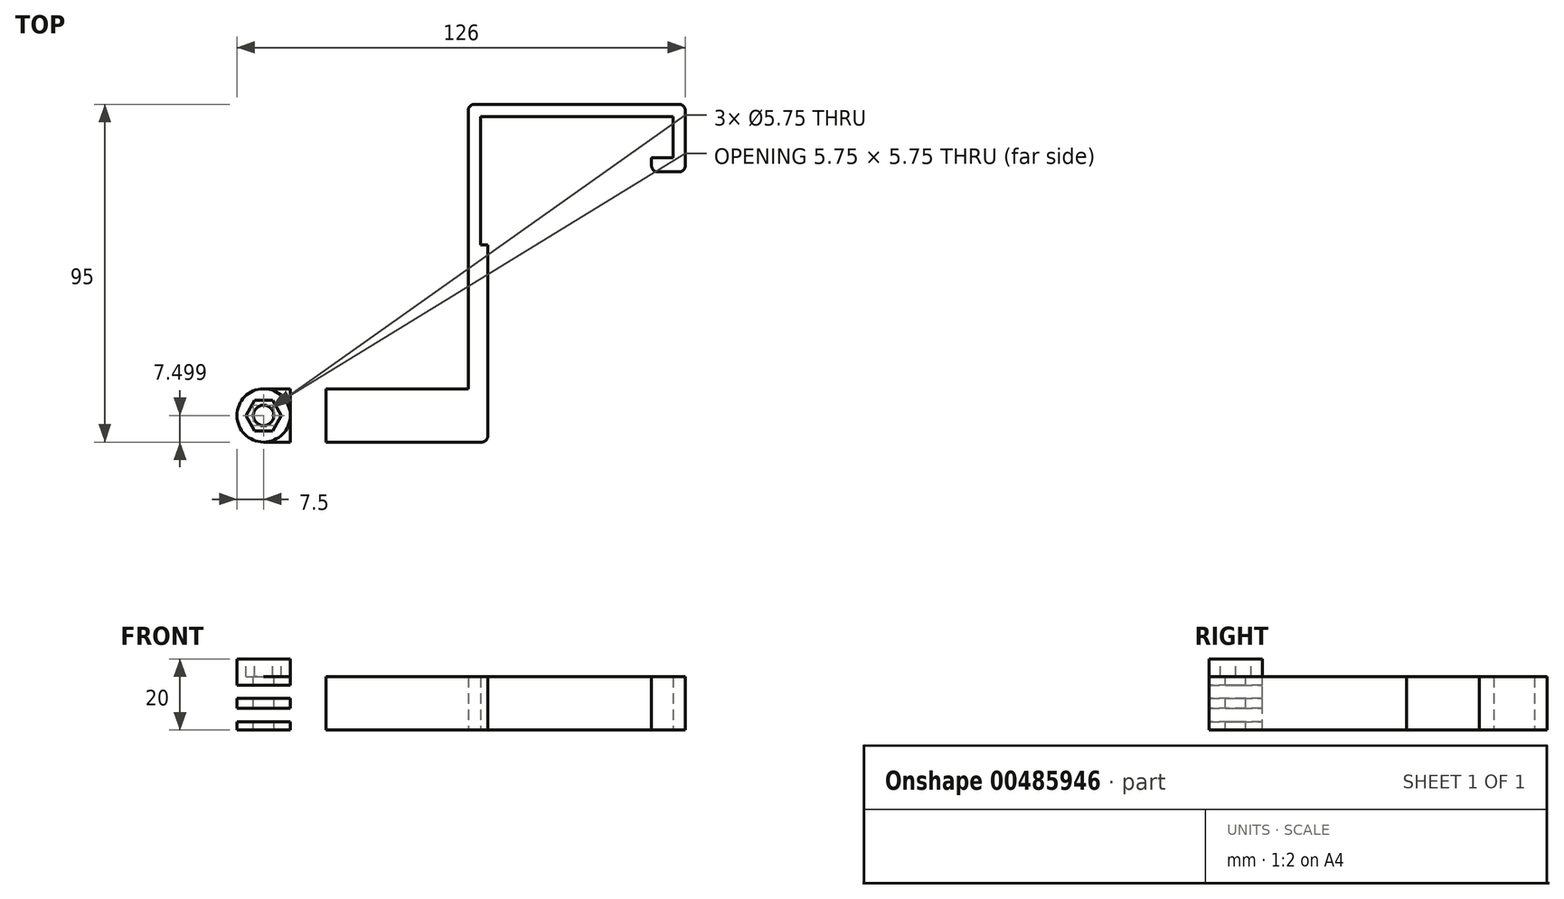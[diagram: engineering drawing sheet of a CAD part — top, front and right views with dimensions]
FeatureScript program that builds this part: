
annotation { "Feature Type Name" : "Feature", "Feature Type Description" : "" }
export const myFeature = defineFeature(function(context is Context, id is Id, definition is map)
    precondition{}
    {
        {
            var Q0;
            Q0=qCreatedBy(makeId("Top.planeOp"),FACE);
            var sketch = newSketch(context, id + "F0", { "sketchPlane" : qUnion([Q0])});
            skLineSegment(sketch, "E0", {"start": v(-30, 3.99) * mm, "end": v(31, 3.99) * mm});
            skLineSegment(sketch, "E1", {"start": v(-26.5, 0.49) * mm, "end": v(27.5, 0.49) * mm});
            skLineSegment(sketch, "E2", {"start": v(27.5, 0.49) * mm, "end": v(27.5, -11.01) * mm});
            skLineSegment(sketch, "E3", {"start": v(-26.5, 0.49) * mm, "end": v(-26.5, -66.01) * mm});
            skLineSegment(sketch, "E4", {"start": v(27.5, -11.01) * mm, "end": v(21.5, -11.01) * mm});
            skLineSegment(sketch, "E5", {"start": v(21.5, -11.01) * mm, "end": v(21.5, -15.01) * mm});
            skLineSegment(sketch, "E6", {"start": v(21.5, -15.01) * mm, "end": v(31, -15.01) * mm});
            skLineSegment(sketch, "E7", {"start": v(31, 3.99) * mm, "end": v(31, -15.01) * mm});
            skLineSegment(sketch, "E8", {"start": v(-26.5, -66.01) * mm, "end": v(-19.5, -66.01) * mm});
            skLineSegment(sketch, "E9", {"start": v(-19.5, -66.01) * mm, "end": v(-19.5, -91.01) * mm});
            skLineSegment(sketch, "E10", {"start": v(-19.5, -91.01) * mm, "end": v(-30, -91.01) * mm});
            skLineSegment(sketch, "E11", {"start": v(-30, 3.99) * mm, "end": v(-30, -91.01) * mm});
            skLineSegment(sketch, "E12", {"start": v(-26.5, -66.01) * mm, "end": v(-26.5, -76.01) * mm});
            skLineSegment(sketch, "E13", {"start": v(-26.5, -76.01) * mm, "end": v(-19.5, -76.01) * mm});
            skLineSegment(sketch, "E14", {"start": v(-26.5, -76.01) * mm, "end": v(-26.5, -91.01) * mm});
            skLineSegment(sketch, "E15", {"start": v(-23, -76.01) * mm, "end": v(-23, -91.01) * mm});
            skLineSegment(sketch, "E16", {"start": v(-23, -66.01) * mm, "end": v(-23, -91.01) * mm});
            skPoint(sketch, "E17.orphan", {"position": v(-23, -101.01) * mm});
            skPoint(sketch, "E18.orphan", {"position": v(-26.5, -101.01) * mm});
            skPoint(sketch, "E19.end.orphan", {"position": v(-19.5, -101.01) * mm});
            skLineSegment(sketch, "E20", {"start": v(-24.5, -66.01) * mm, "end": v(-24.5, -91.01) * mm});
            skSolve(sketch);
        }
        {
            var Q0;
            {var subQ0=sQuery(id+"F0.wireOp",EDGE,"E12");Q0=makeQuery(id+"F0.imprint","IMPRINT",FACE,{"disambiguationData":[TD([[makeQuery(id+"F0.imprint","IMPRINT",EDGE,{"derivedFrom":subQ0}),1.0]])]});}
            var Q1;
            Q1=makeQuery(id+"F0.imprint","IMPRINT",FACE,{"disambiguationData":[TD([[makeQuery(id+"F0.imprint","IMPRINT",EDGE,{"derivedFrom":sQuery(id+"F0.wireOp",EDGE,"E0")}),-1.0]])]});
            var Q2;
            {var subQ0=sQuery(id+"F0.wireOp",EDGE,"E14");Q2=makeQuery(id+"F0.imprint","IMPRINT",FACE,{"disambiguationData":[TD([[makeQuery(id+"F0.imprint","IMPRINT",EDGE,{"derivedFrom":subQ0}),1.0]])]});}
            extrude(context, id + "F1", {"entities" : qUnion([Q0, Q1, Q2]), "depth" : 15 * mm});
        }
        {
            var Q0;
            Q0=makeQuery(id+"F1.opExtrude","SWEPT_FACE",FACE,{"disambiguationData":[OSD([sQuery(id+"F0.wireOp",EDGE,"E11")])]});
            var sketch = newSketch(context, id + "F2", { "sketchPlane" : qUnion([Q0])});
            skLineSegment(sketch, "E21.bottom", {"start": v(91.01, 0) * mm, "end": v(76.01, 0) * mm});
            skLineSegment(sketch, "E21.top", {"start": v(91.01, 15) * mm, "end": v(76.01, 15) * mm});
            skLineSegment(sketch, "E21.left", {"start": v(91.01, 0) * mm, "end": v(91.01, 15) * mm});
            skLineSegment(sketch, "E21.right", {"start": v(76.01, 0) * mm, "end": v(76.01, 15) * mm});
            skSolve(sketch);
        }
        {
            var Q0;
            Q0=makeQuery(id+"F2.imprint","IMPRINT",FACE,{"disambiguationData":[TD([[makeQuery(id+"F2.imprint","IMPRINT",EDGE,{"derivedFrom":sQuery(id+"F2.wireOp",EDGE,"E21.bottom")}),1.0]])]});
            extrude(context, id + "F3", {"entities" : qUnion([Q0]), "operationType" : NewBodyOperationType.ADD, "depth" : 65 * mm});
        }
        {
            var Q0;
            Q0=makeQuery(id+"F3.boolean.opBoolean","MERGE",FACE,{"derivedFrom":[makeQuery(id+"F1.opExtrude","CAP_FACE",FACE,{"disambiguationData":[OSD([sQuery(id+"F0.wireOp",EDGE,"E0"),sQuery(id+"F0.wireOp",EDGE,"E1"),sQuery(id+"F0.wireOp",EDGE,"E2"),sQuery(id+"F0.wireOp",EDGE,"E3"),sQuery(id+"F0.wireOp",EDGE,"E4"),sQuery(id+"F0.wireOp",EDGE,"E5"),sQuery(id+"F0.wireOp",EDGE,"E6"),sQuery(id+"F0.wireOp",EDGE,"E7"),sQuery(id+"F0.wireOp",EDGE,"E8"),sQuery(id+"F0.wireOp",EDGE,"E9"),sQuery(id+"F0.wireOp",EDGE,"E10"),sQuery(id+"F0.wireOp",EDGE,"E11"),sQuery(id+"F0.wireOp",EDGE,"E13"),sQuery(id+"F0.wireOp",EDGE,"E19"),sQuery(id+"F0.wireOp",EDGE,"E15")])],"isStart":false}),makeQuery(id+"F3.opExtrude","SWEPT_FACE",FACE,{"disambiguationData":[OSD([sQuery(id+"F2.wireOp",EDGE,"E21.top")])]})]});
            var sketch = newSketch(context, id + "F4", { "sketchPlane" : qUnion([Q0])});
            skLineSegment(sketch, "E22", {"start": v(-30, -76.01) * mm, "end": v(-30, -91.01) * mm});
            skLineSegment(sketch, "E23", {"start": v(-95, -83.51) * mm, "end": v(-87.5, -83.51) * mm});
            skCircle(sketch, "E24", {"center": v(-87.5, -83.51) * mm, "radius": 2.88 * mm});
            skCircle(sketch, "E25", {"center": v(-87.5, -83.51) * mm, "radius": 7.5 * mm});
            skSolve(sketch);
        }
        {
            var Q0;
            {var subQ0=sQuery(id+"F4.wireOp",EDGE,"E25");var subQ1=sQuery(id+"F2.wireOp",EDGE,"E21.top");var subQ2=makeQuery(id+"F3.opExtrude","CAP_EDGE",EDGE,{"disambiguationData":[OSD([subQ1])],"isStart":false});var subQ3=makeQuery(id+"F4.imprint","INTERSECT",VERTEX,{"derivedFrom":[subQ2,subQ0]});Q0=makeQuery(id+"F4.imprint","IMPRINT",FACE,{"disambiguationData":[TD([[makeQuery(id+"F4.imprint","IMPRINT",EDGE,{"disambiguationData":[TD([[subQ3,1.0]])],"derivedFrom":subQ0}),-1.0]])]});}
            var Q1;
            {var subQ0=sQuery(id+"F4.wireOp",EDGE,"E25");var subQ1=sQuery(id+"F2.wireOp",EDGE,"E21.top");var subQ2=makeQuery(id+"F3.opExtrude","CAP_EDGE",EDGE,{"disambiguationData":[OSD([subQ1])],"isStart":false});var subQ3=makeQuery(id+"F4.imprint","INTERSECT",VERTEX,{"derivedFrom":[subQ2,subQ0]});Q1=makeQuery(id+"F4.imprint","IMPRINT",FACE,{"disambiguationData":[TD([[makeQuery(id+"F4.imprint","IMPRINT",EDGE,{"disambiguationData":[TD([[subQ3,-1.0]])],"derivedFrom":subQ0}),-1.0]])]});}
            extrude(context, id + "F5", {"entities" : qUnion([Q0, Q1]), "operationType" : NewBodyOperationType.REMOVE, "oppositeDirection" : true, "depth" : 25 * mm});
        }
        {
            var Q0;
            Q0=makeQuery(id+"F4.imprint","IMPRINT",FACE,{"disambiguationData":[TD([[makeQuery(id+"F4.imprint","IMPRINT",EDGE,{"derivedFrom":sQuery(id+"F4.wireOp",EDGE,"E24")}),-1.0]])]});
            extrude(context, id + "F6", {"entities" : qUnion([Q0]), "operationType" : NewBodyOperationType.ADD, "depth" : 5 * mm});
        }
        {
            var Q0;
            Q0=makeQuery(id+"F6.opExtrude","CAP_FACE",FACE,{"disambiguationData":[OSD([sQuery(id+"F4.wireOp",EDGE,"E24"),sQuery(id+"F4.wireOp",EDGE,"E25")])],"isStart":false});
            var sketch = newSketch(context, id + "F7", { "sketchPlane" : qUnion([Q0])});
            skCircle(sketch, "E26.cCircle", {"center": v(-87.5, -83.51) * mm, "radius": 4.33 * mm, "construction": true});
            skLineSegment(sketch, "E26.0", {"start": v(-90, -79.18) * mm, "end": v(-85, -79.18) * mm});
            skLineSegment(sketch, "E26.1", {"start": v(-85, -79.18) * mm, "end": v(-82.5, -83.51) * mm});
            skLineSegment(sketch, "E26.2", {"start": v(-82.5, -83.51) * mm, "end": v(-85, -87.84) * mm});
            skLineSegment(sketch, "E26.3", {"start": v(-85, -87.84) * mm, "end": v(-90, -87.84) * mm});
            skLineSegment(sketch, "E26.4", {"start": v(-90, -87.84) * mm, "end": v(-92.5, -83.51) * mm});
            skLineSegment(sketch, "E26.5", {"start": v(-92.5, -83.51) * mm, "end": v(-90, -79.18) * mm});
            skPoint(sketch, "E26.0.midPoint", {"position": v(-87.5, -79.18) * mm});
            skSolve(sketch);
        }
        {
            var Q0;
            Q0=makeQuery(id+"F7.imprint","IMPRINT",FACE,{"disambiguationData":[TD([[makeQuery(id+"F7.imprint","IMPRINT",EDGE,{"derivedFrom":sQuery(id+"F7.wireOp",EDGE,"E26.0")}),-1.0]])]});
            extrude(context, id + "F8", {"entities" : qUnion([Q0]), "operationType" : NewBodyOperationType.REMOVE, "oppositeDirection" : true, "depth" : 5 * mm});
        }
        {
            var Q0;
            Q0=makeQuery(id+"F4.imprint","IMPRINT",FACE,{"disambiguationData":[TD([[makeQuery(id+"F4.imprint","IMPRINT",EDGE,{"derivedFrom":sQuery(id+"F4.wireOp",EDGE,"E24")}),1.0]])]});
            extrude(context, id + "F9", {"entities" : qUnion([Q0]), "operationType" : NewBodyOperationType.REMOVE, "oppositeDirection" : true, "depth" : 25 * mm});
        }
        {
            var Q0;
            Q0=makeQuery(id+"F3.boolean.opBoolean","MERGE",FACE,{"derivedFrom":[makeQuery(id+"F1.opExtrude","SWEPT_FACE",FACE,{"disambiguationData":[OSD([sQuery(id+"F0.wireOp",EDGE,"E10")])]}),makeQuery(id+"F3.opExtrude","SWEPT_FACE",FACE,{"disambiguationData":[OSD([sQuery(id+"F2.wireOp",EDGE,"E21.left")])]})]});
            var sketch = newSketch(context, id + "F10", { "sketchPlane" : qUnion([Q0])});
            skLineSegment(sketch, "E27.bottom", {"start": v(-80, 15) * mm, "end": v(-95, 15) * mm});
            skLineSegment(sketch, "E27.top", {"start": v(-80, 0) * mm, "end": v(-95, 0) * mm});
            skLineSegment(sketch, "E27.left", {"start": v(-80, 15) * mm, "end": v(-80, 0) * mm});
            skLineSegment(sketch, "E27.right", {"start": v(-95, 15) * mm, "end": v(-95, 0) * mm});
            skLineSegment(sketch, "E28", {"start": v(-95, 12.6) * mm, "end": v(-80, 12.6) * mm});
            skLineSegment(sketch, "E29.bottom", {"start": v(-95, 8.9) * mm, "end": v(-80, 8.9) * mm});
            skLineSegment(sketch, "E29.top", {"start": v(-95, 6.1) * mm, "end": v(-80, 6.1) * mm});
            skLineSegment(sketch, "E29.left", {"start": v(-95, 8.9) * mm, "end": v(-95, 6.1) * mm});
            skLineSegment(sketch, "E29.right", {"start": v(-80, 8.9) * mm, "end": v(-80, 6.1) * mm});
            skLineSegment(sketch, "E30", {"start": v(-95, 2.4) * mm, "end": v(-80, 2.4) * mm});
            skLineSegment(sketch, "E31.bottom", {"start": v(-80, 15) * mm, "end": v(-65, 15) * mm});
            skLineSegment(sketch, "E31.top", {"start": v(-80, 0) * mm, "end": v(-65, 0) * mm});
            skLineSegment(sketch, "E32", {"start": v(-80, 12.6) * mm, "end": v(-65, 12.6) * mm});
            skLineSegment(sketch, "E33", {"start": v(-80, 8.9) * mm, "end": v(-65, 8.9) * mm});
            skLineSegment(sketch, "E34", {"start": v(-80, 6.1) * mm, "end": v(-65, 6.1) * mm});
            skLineSegment(sketch, "E35", {"start": v(-80, 2.4) * mm, "end": v(-65, 2.4) * mm});
            skLineSegment(sketch, "E36.MirrorCS", {"start": v(-65, 8.9) * mm, "end": v(-65, 6.1) * mm});
            skLineSegment(sketch, "E37.MirrorCS", {"start": v(-65, 15) * mm, "end": v(-65, 0) * mm});
            skLineSegment(sketch, "E38.MirrorCS", {"start": v(-65, 12.6) * mm, "end": v(-80, 12.6) * mm});
            skLineSegment(sketch, "E39.MirrorCS", {"start": v(-65, 6.1) * mm, "end": v(-80, 6.1) * mm});
            skLineSegment(sketch, "E40.MirrorCS", {"start": v(-65, 2.4) * mm, "end": v(-80, 2.4) * mm});
            skLineSegment(sketch, "E41.MirrorCS", {"start": v(-65, 8.9) * mm, "end": v(-80, 8.9) * mm});
            skLineSegment(sketch, "E42", {"start": v(-70, 15) * mm, "end": v(-70, 0) * mm});
            skLineSegment(sketch, "E43", {"start": v(-95, 7.5) * mm, "end": v(-90.9, 7.5) * mm});
            skSolve(sketch);
        }
        {
            var Q0;
            {var subQ0=sQuery(id+"F10.wireOp",EDGE,"E38.MirrorCS");var subQ5=sQuery(id+"F10.wireOp",EDGE,"E42");var subQ6=makeQuery(id+"F10.imprint","INTERSECT",VERTEX,{"derivedFrom":[subQ0,subQ5]});Q0=makeQuery(id+"F10.imprint","IMPRINT",FACE,{"disambiguationData":[TD([[makeQuery(id+"F10.imprint","IMPRINT",EDGE,{"disambiguationData":[TD([[subQ6,-1.0]])],"derivedFrom":subQ5}),-1.0]])]});}
            var Q1;
            {var subQ0=sQuery(id+"F10.wireOp",EDGE,"E27.right");var subQ1=sQuery(id+"F10.wireOp",EDGE,"E28");var subQ2=makeQuery(id+"F10.imprint","INTERSECT",VERTEX,{"derivedFrom":[subQ1,subQ0]});Q1=makeQuery(id+"F10.imprint","IMPRINT",FACE,{"disambiguationData":[TD([[makeQuery(id+"F10.imprint","IMPRINT",EDGE,{"disambiguationData":[TD([[subQ2,-1.0]])],"derivedFrom":subQ0}),1.0]])]});}
            var Q2;
            {var subQ0=sQuery(id+"F10.wireOp",EDGE,"E27.left");var subQ1=sQuery(id+"F10.wireOp",EDGE,"E28");var subQ2=makeQuery(id+"F10.imprint","INTERSECT",VERTEX,{"derivedFrom":[subQ1,subQ0,sQuery(id+"F10.wireOp",EDGE,"E38.MirrorCS")]});Q2=makeQuery(id+"F10.imprint","IMPRINT",FACE,{"disambiguationData":[TD([[makeQuery(id+"F10.imprint","IMPRINT",EDGE,{"disambiguationData":[TD([[subQ2,-1.0]])],"derivedFrom":subQ0}),-1.0]])]});}
            var Q3;
            {var subQ0=sQuery(id+"F10.wireOp",EDGE,"E27.left");var subQ1=sQuery(id+"F10.wireOp",EDGE,"E29.top");var subQ2=makeQuery(id+"F10.imprint","INTERSECT",VERTEX,{"derivedFrom":[subQ1,subQ0,sQuery(id+"F10.wireOp",EDGE,"E39.MirrorCS")]});Q3=makeQuery(id+"F10.imprint","IMPRINT",FACE,{"disambiguationData":[TD([[makeQuery(id+"F10.imprint","IMPRINT",EDGE,{"disambiguationData":[TD([[subQ2,-1.0]])],"derivedFrom":subQ0}),-1.0]])]});}
            var Q4;
            {var subQ0=sQuery(id+"F10.wireOp",EDGE,"E27.right");var subQ1=sQuery(id+"F10.wireOp",EDGE,"E29.top");var subQ2=makeQuery(id+"F10.imprint","INTERSECT",VERTEX,{"derivedFrom":[subQ1,subQ0]});Q4=makeQuery(id+"F10.imprint","IMPRINT",FACE,{"disambiguationData":[TD([[makeQuery(id+"F10.imprint","IMPRINT",EDGE,{"disambiguationData":[TD([[subQ2,-1.0]])],"derivedFrom":subQ0}),1.0]])]});}
            var Q5;
            {var subQ0=sQuery(id+"F10.wireOp",EDGE,"E39.MirrorCS");var subQ5=sQuery(id+"F10.wireOp",EDGE,"E42");var subQ6=makeQuery(id+"F10.imprint","INTERSECT",VERTEX,{"derivedFrom":[subQ0,subQ5]});Q5=makeQuery(id+"F10.imprint","IMPRINT",FACE,{"disambiguationData":[TD([[makeQuery(id+"F10.imprint","IMPRINT",EDGE,{"disambiguationData":[TD([[subQ6,-1.0]])],"derivedFrom":subQ5}),-1.0]])]});}
            extrude(context, id + "F11", {"entities" : qUnion([Q0, Q1, Q2, Q3, Q4, Q5]), "operationType" : NewBodyOperationType.REMOVE, "oppositeDirection" : true, "depth" : 25 * mm});
        }
        {
            var Q0;
            Q0=makeQuery(id+"F1.opExtrude","SWEPT_FACE",FACE,{"disambiguationData":[OSD([sQuery(id+"F0.wireOp",EDGE,"E3")])]});
            var sketch = newSketch(context, id + "F12", { "sketchPlane" : qUnion([Q0])});
            skLineSegment(sketch, "E44.bottom", {"start": v(-66.01, 15) * mm, "end": v(-35.51, 15) * mm});
            skLineSegment(sketch, "E44.top", {"start": v(-66.01, 0) * mm, "end": v(-35.51, 0) * mm});
            skLineSegment(sketch, "E44.left", {"start": v(-66.01, 15) * mm, "end": v(-66.01, 0) * mm});
            skLineSegment(sketch, "E44.right", {"start": v(-35.51, 15) * mm, "end": v(-35.51, 0) * mm});
            skSolve(sketch);
        }
        {
            var Q0;
            Q0=makeQuery(id+"F12.imprint","IMPRINT",FACE,{"disambiguationData":[TD([[makeQuery(id+"F12.imprint","IMPRINT",EDGE,{"derivedFrom":sQuery(id+"F12.wireOp",EDGE,"E44.bottom")}),1.0]])]});
            extrude(context, id + "F13", {"entities" : qUnion([Q0]), "operationType" : NewBodyOperationType.ADD, "depth" : 2 * mm});
        }
        {
            var Q0;
            Q0=makeQuery(id+"F1.opExtrude","SWEPT_EDGE",EDGE,{"disambiguationData":[OSD([sQuery(id+"F0.wireOp",EDGE,"E19"),sQuery(id+"F0.wireOp",EDGE,"E16")])]});
            var Q1;
            Q1=makeQuery(id+"F1.opExtrude","SWEPT_EDGE",EDGE,{"disambiguationData":[OSD([sQuery(id+"F0.wireOp",EDGE,"E9"),sQuery(id+"F0.wireOp",EDGE,"E19")])]});
            var Q2;
            Q2=makeQuery(id+"F1.opExtrude","SWEPT_EDGE",EDGE,{"disambiguationData":[OSD([sQuery(id+"F0.wireOp",EDGE,"E9"),sQuery(id+"F0.wireOp",EDGE,"E10")])]});
            var Q3;
            Q3=makeQuery(id+"F3.opExtrude","CAP_EDGE",EDGE,{"disambiguationData":[OSD([sQuery(id+"F2.wireOp",EDGE,"E21.right")])],"isStart":true});
            var Q4;
            Q4=makeQuery(id+"F1.opExtrude","SWEPT_EDGE",EDGE,{"disambiguationData":[OSD([sQuery(id+"F0.wireOp",EDGE,"E0"),sQuery(id+"F0.wireOp",EDGE,"E11")])]});
            var Q5;
            Q5=makeQuery(id+"F1.opExtrude","SWEPT_EDGE",EDGE,{"disambiguationData":[OSD([sQuery(id+"F0.wireOp",EDGE,"E0"),sQuery(id+"F0.wireOp",EDGE,"E7")])]});
            var Q6;
            Q6=makeQuery(id+"F1.opExtrude","SWEPT_EDGE",EDGE,{"disambiguationData":[OSD([sQuery(id+"F0.wireOp",EDGE,"E6"),sQuery(id+"F0.wireOp",EDGE,"E7")])]});
            var Q7;
            Q7=makeQuery(id+"F1.opExtrude","SWEPT_EDGE",EDGE,{"disambiguationData":[OSD([sQuery(id+"F0.wireOp",EDGE,"E5"),sQuery(id+"F0.wireOp",EDGE,"E6")])]});
            fillet(context, id + "F14", {"entities" : qUnion([Q0, Q1, Q2, Q3, Q4, Q5, Q6, Q7]), "radius" : 1.75 * mm, "tangentPropagation" : true, "allowEdgeOverflow" : false});
        }
    });
